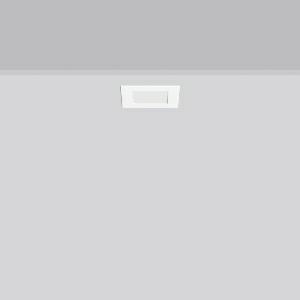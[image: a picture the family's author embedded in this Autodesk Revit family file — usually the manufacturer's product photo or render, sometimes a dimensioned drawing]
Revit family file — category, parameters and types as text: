
# Revit family: toledo_flat_square_e_672241_002_1_89_de5d
name_source: partatom
category: Lighting Fixtures
units: mm (PartAtom-declared; Revit-internal decimal feet)

## family parameters
Cut with Voids When Loaded = No
Host = Face
Light Source = No
Part Type = Normal
Room Calculation Point = No
Round Connector Dimension = Use Diameter
Shared = No

## types (1)
- TOLEDO FLAT square E (1 x LED Modul 840, 380 lm, 4000)
    Apparent Load = 6 VA
    CIE Flux Codes = 49 80 96 100 100
    Color Rendering = 80
    Color Temperature = 4000
    Default Elevation = 1800 mm
    Description = Series: TOLEDO FLAT square
Square recessed downlight. For escape route illumination. Housing: die-cast aluminium, powder-coated. Lightguide and diffuser made of non-yellowing plastic (PMMA). Diffuser opal matt plastic. Ceiling installation with spring system. Including separate LED converter with connecting cable 250 mm. Suitable for connection to central battery systems. With AC Control monitoring module for LUXIFAIR central battery units. External driver with simple plug-in locking system. 
Colour: white
Length: 110 mm
Width: 110 mm
Height: 3 mm
Cut-out length: 96 mm
Cut-out width: 96 mm
Recess height: 100 mm
Luminaire: recess height: 37-57 mm
Weight: 1.03 kg
Operating mode: maintained power mode
Lamp: LED
Socket: without socket
Colour temperature: 4000K
Colour rendering index (CRI): 80
System power: 5.7 W
Rated luminous flux: 380 lm
Luminous flux, emergency: 380 lm
System power, emergency: 5.7 W
Control gear: Regulated power supply
Protection class: I
Type of protection: IP 54
    Height = 0 mm  [stored 0 ft]
    Lamp = 1 x LED Modul 840
    Lamp Light Flux = 380 lm
    Lamp count = 1
    Length = 110 mm
    Lifetime = 50000 h
    Luminous efficacy = 67 lm/W
    Manufacturer = RZB
    ModVariant = No
    Model = 672241.002.1.89
    Mounting Place = Ceiling
    Mounting Type = Recessed
    Number of Poles = 1
    OnlyDefault = Yes
    Power Factor = 1
    Product Name = TOLEDO FLAT square E
    Product group = Recessed downlights
    ProductGroupID = 402
    Protection Class = Protection class I
    Protection Degree = IP 40
    RLX_Detail_Level = 1
    RLX_Emergency_Light_Flux = 380 lm
    RLX_Emergency_Type = 3
    RLX_Emergency_Type_DB = Yes
    RlxData = <blob elided: 9765 chars, md5=26bc906f>
    Socket = socket
    Standby Power = 0 W
    System Light Flux = 380 lm
    System Power = 6 W
    Type Comments = Product without accessories
    Type Image = 901485.002.jpg
    URL = http://relux.com
    VarID = ---
    Voltage = 230 V
    Voltage Range = 220-240 V
    Weight = 0.00 kg
    Width = 110 mm

note: [stored X ft] marks values corroborated as IEEE doubles in the binary element streams (Revit-internal decimal feet)

## geometry (parser evidence)
native form markers: Sweep x9
no freeform markers — native parametric forms only
